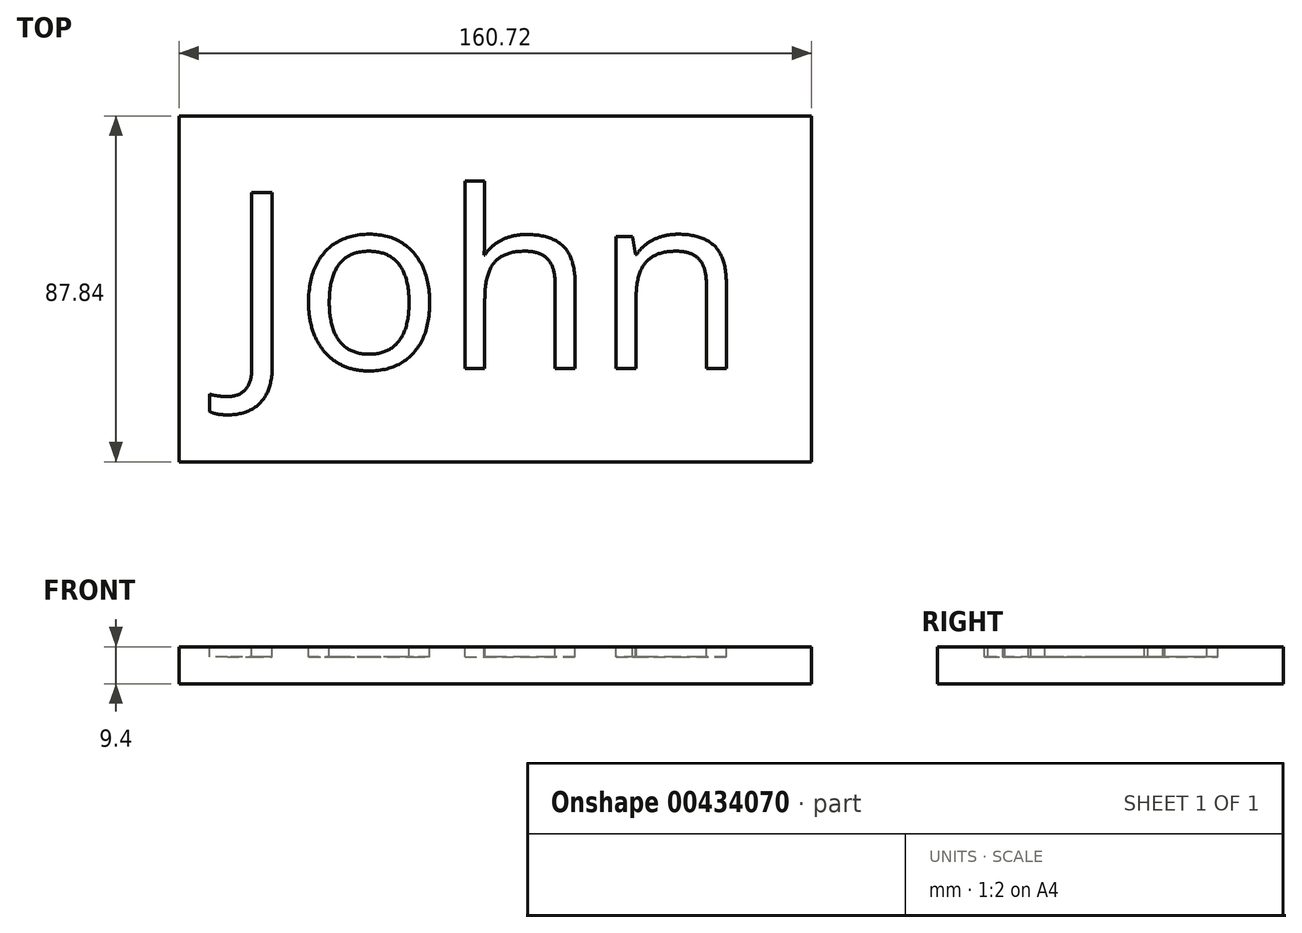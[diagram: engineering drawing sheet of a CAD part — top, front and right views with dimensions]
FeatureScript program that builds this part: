
annotation { "Feature Type Name" : "Feature", "Feature Type Description" : "" }
export const myFeature = defineFeature(function(context is Context, id is Id, definition is map)
    precondition{}
    {
        {
            var Q0;
            Q0=qCreatedBy(makeId("Top.planeOp"),FACE);
            var sketch = newSketch(context, id + "F0", { "sketchPlane" : qUnion([Q0])});
            skLineSegment(sketch, "E0.bottom", {"start": v(-71.99, 47.06) * mm, "end": v(88.73, 47.06) * mm});
            skLineSegment(sketch, "E0.top", {"start": v(-71.99, -40.78) * mm, "end": v(88.73, -40.78) * mm});
            skLineSegment(sketch, "E0.left", {"start": v(-71.99, 47.06) * mm, "end": v(-71.99, -40.78) * mm});
            skLineSegment(sketch, "E0.right", {"start": v(88.73, 47.06) * mm, "end": v(88.73, -40.78) * mm});
            skLineSegment(sketch, "E1.bottom", {"start": v(-71.99, 47.06) * mm, "end": v(25.4, 47.06) * mm});
            skLineSegment(sketch, "E1.left", {"start": v(-71.99, 47.06) * mm, "end": v(-71.99, -34.57) * mm});
            skSolve(sketch);
        }
        {
            var Q0;
            Q0=makeQuery(id+"F0.imprint","IMPRINT",FACE,{"disambiguationData":[TD([[makeQuery(id+"F0.imprint","IMPRINT",EDGE,{"derivedFrom":sQuery(id+"F0.wireOp",EDGE,"E0.bottom")}),-1.0]])]});
            extrude(context, id + "F1", {"entities" : qUnion([Q0]), "depth" : 9.4 * mm});
        }
        {
            var Q0;
            Q0=makeQuery(id+"F1.opExtrude","CAP_FACE",FACE,{"disambiguationData":[OSD([sQuery(id+"F0.wireOp",EDGE,"E0.bottom"),sQuery(id+"F0.wireOp",EDGE,"E0.top"),sQuery(id+"F0.wireOp",EDGE,"E0.left"),sQuery(id+"F0.wireOp",EDGE,"E0.right"),sQuery(id+"F0.wireOp",EDGE,"E1.bottom"),sQuery(id+"F0.wireOp",EDGE,"E1.left")])],"isStart":false});
            var sketch = newSketch(context, id + "F2", { "sketchPlane" : qUnion([Q0])});
            skText(sketch, "E2", { "text": "John", "fontName": "OpenSans-Regular.ttf"});
            const initialGuessF2  = {"E2": [-0.05929, -0.01708, 1, 0, 0.04508]};
            skSetInitialGuess(sketch, initialGuessF2);
            skSolve(sketch);
        }
        {
            var Q0;
            Q0 = qSketchRegion(id + "F2", true);
            extrude(context, id + "F3", {"entities" : qUnion([Q0]), "operationType" : NewBodyOperationType.REMOVE, "oppositeDirection" : true, "depth" : 2.54 * mm});
        }
    });
